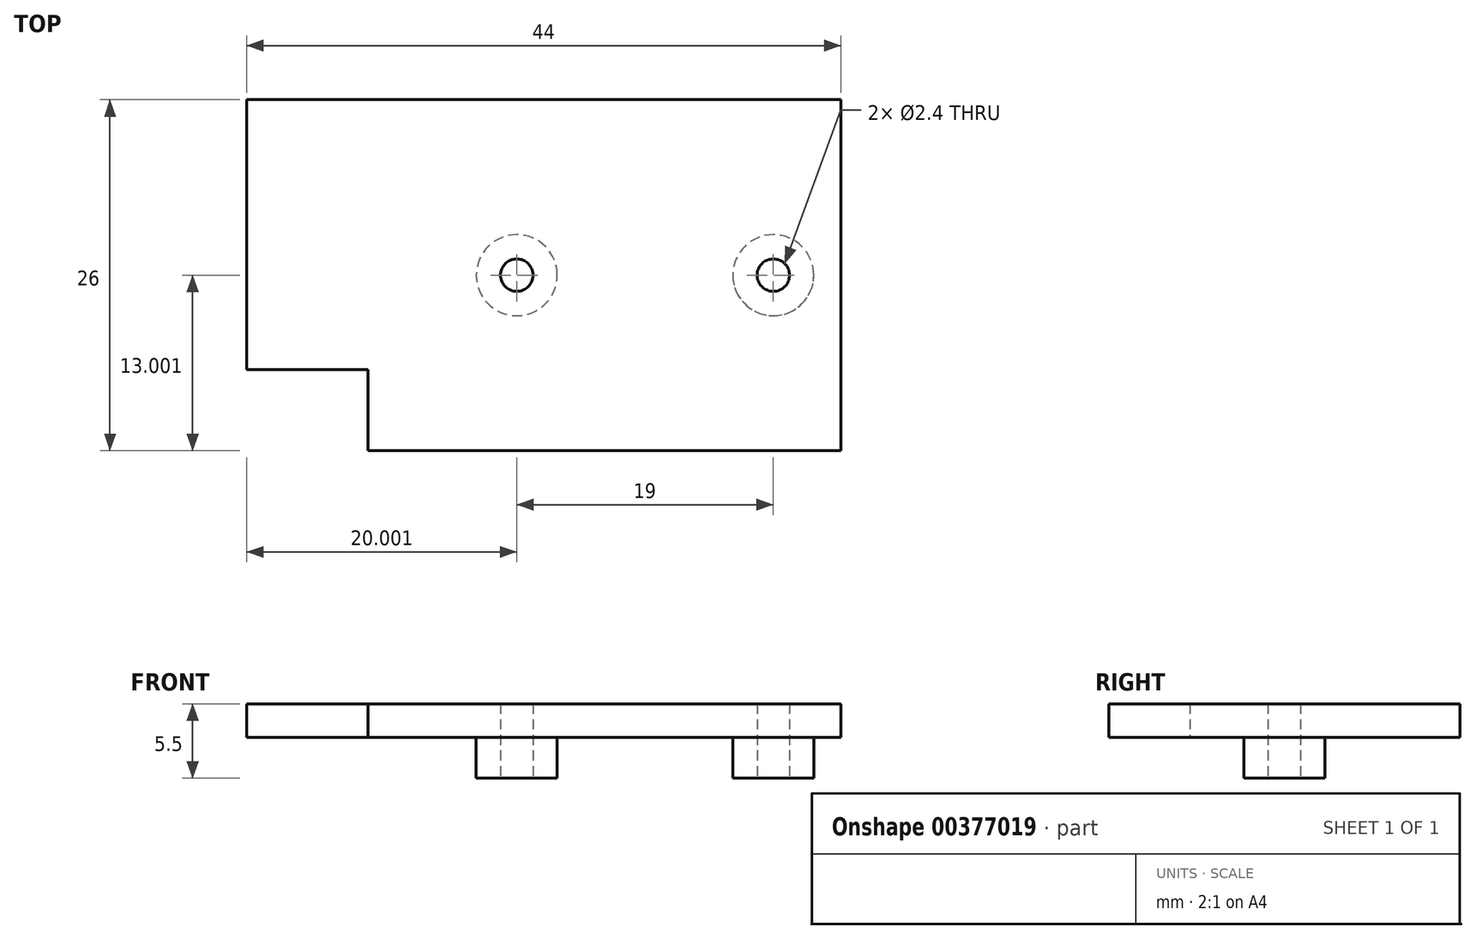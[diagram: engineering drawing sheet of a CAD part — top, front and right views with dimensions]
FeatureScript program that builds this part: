
annotation { "Feature Type Name" : "Feature", "Feature Type Description" : "" }
export const myFeature = defineFeature(function(context is Context, id is Id, definition is map)
    precondition{}
    {
        {
            var Q0;
            Q0=qCreatedBy(makeId("Top.planeOp"),FACE);
            var sketch = newSketch(context, id + "F0", { "sketchPlane" : qUnion([Q0])});
            skLineSegment(sketch, "E0.bottom", {"start": v(-14.89, -7.06) * mm, "end": v(20.11, -7.06) * mm});
            skLineSegment(sketch, "E0.top", {"start": v(-14.89, 18.94) * mm, "end": v(20.11, 18.94) * mm});
            skLineSegment(sketch, "E0.left", {"start": v(-14.89, -7.06) * mm, "end": v(-14.89, 18.94) * mm});
            skLineSegment(sketch, "E0.right", {"start": v(20.11, -7.06) * mm, "end": v(20.11, 18.94) * mm});
            skCircle(sketch, "E1", {"center": v(15.11, 5.94) * mm, "radius": 1.2 * mm});
            skCircle(sketch, "E2", {"center": v(-3.89, 5.94) * mm, "radius": 1.2 * mm});
            skSolve(sketch);
        }
        {
            var Q0;
            Q0=makeQuery(id+"F0.imprint","IMPRINT",FACE,{"disambiguationData":[TD([[makeQuery(id+"F0.imprint","IMPRINT",EDGE,{"derivedFrom":sQuery(id+"F0.wireOp",EDGE,"E0.bottom")}),1.0]])]});
            extrude(context, id + "F1", {"entities" : qUnion([Q0]), "depth" : 2.5 * mm});
        }
        {
            var Q0;
            Q0=makeQuery(id+"F1.opExtrude","CAP_FACE",FACE,{"disambiguationData":[OSD([sQuery(id+"F0.wireOp",EDGE,"E0.bottom"),sQuery(id+"F0.wireOp",EDGE,"E0.top"),sQuery(id+"F0.wireOp",EDGE,"E0.left"),sQuery(id+"F0.wireOp",EDGE,"E0.right"),sQuery(id+"F0.wireOp",EDGE,"E1"),sQuery(id+"F0.wireOp",EDGE,"E2")])],"isStart":true});
            var sketch = newSketch(context, id + "F2", { "sketchPlane" : qUnion([Q0])});
            skCircle(sketch, "E3", {"center": v(-3.89, -5.94) * mm, "radius": 3 * mm});
            skCircle(sketch, "E4", {"center": v(15.11, -5.94) * mm, "radius": 3 * mm});
            skSolve(sketch);
        }
        {
            var Q0;
            Q0 = qSketchRegion(id + "F2", true);
            extrude(context, id + "F3", {"entities" : qUnion([Q0]), "operationType" : NewBodyOperationType.ADD, "depth" : 3 * mm});
        }
        {
            var Q0;
            Q0=makeQuery(id+"F3.opExtrude","CAP_FACE",FACE,{"disambiguationData":[OSD([sQuery(id+"F2.wireOp",EDGE,"E3")])],"isStart":true});
            extrude(context, id + "F4", {"entities" : qUnion([Q0]), "operationType" : NewBodyOperationType.REMOVE, "oppositeDirection" : true, "depth" : 25 * mm});
        }
        {
            var Q0;
            Q0=makeQuery(id+"F3.opExtrude","CAP_FACE",FACE,{"disambiguationData":[OSD([sQuery(id+"F2.wireOp",EDGE,"E4")])],"isStart":true});
            extrude(context, id + "F5", {"entities" : qUnion([Q0]), "operationType" : NewBodyOperationType.REMOVE, "oppositeDirection" : true, "depth" : 25 * mm});
        }
        {
            var Q0;
            Q0=makeQuery(id+"F1.opExtrude","SWEPT_FACE",FACE,{"disambiguationData":[OSD([sQuery(id+"F0.wireOp",EDGE,"E0.left")])]});
            var sketch = newSketch(context, id + "F6", { "sketchPlane" : qUnion([Q0])});
            skLineSegment(sketch, "E5.bottom", {"start": v(-18.94, 2.5) * mm, "end": v(1.06, 2.5) * mm});
            skLineSegment(sketch, "E5.top", {"start": v(-18.94, 0) * mm, "end": v(1.06, 0) * mm});
            skLineSegment(sketch, "E5.left", {"start": v(-18.94, 2.5) * mm, "end": v(-18.94, 0) * mm});
            skLineSegment(sketch, "E5.right", {"start": v(1.06, 2.5) * mm, "end": v(1.06, 0) * mm});
            skSolve(sketch);
        }
        {
            var Q0;
            Q0 = qSketchRegion(id + "F6", true);
            extrude(context, id + "F7", {"entities" : qUnion([Q0]), "operationType" : NewBodyOperationType.ADD, "depth" : 9 * mm});
        }
    });
